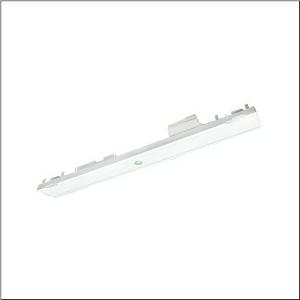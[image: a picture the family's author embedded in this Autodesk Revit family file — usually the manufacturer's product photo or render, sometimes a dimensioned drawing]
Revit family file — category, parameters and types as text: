
# Revit family: licross_r_56tl1e7c4x31_1f0a
name_source: partatom
category: Lighting Fixtures
units: mm (PartAtom-declared; Revit-internal decimal feet)

## family parameters
Cut with Voids When Loaded = No
Host = Face
Light Source = No
Part Type = Normal
Room Calculation Point = No
Round Connector Dimension = Use Diameter
Shared = No

## types (1)
- Licross® (1 x LED, 320 lm, 3.9 W, 4000K)
    Apparent Load = 4 VA
    CIE Flux Codes = 63 91 97 100 100
    Color Rendering = 70
    Color Temperature = 4000K
    Default Elevation = 1800 mm
    Description = Licross®, luminaire insert, of sheet steel, coil coated, white, length: 500mm, width: 59mm, height: 60mm, mounting height: 7..17m, emergency light element,LED rated luminous flux: 320lm, light colour: 740, control gear: CEAG, with plug, 6-pole, with phase selection, mains connection: 220..240V, AC/DC, 0/50..60Hz, rated input power: 3.9W, internal wiring halogen-free, for trunking rail, 9..14-core, for emergency light function, supply monitoring module CEAG, with address switch, choice between two emergency light lines via tool-free moving of contact pin prior to installation in trunking rail, primary light control with lens, of PMMA, primary optical cover: cover, of PMMA, light emission: direct distribution, primary light characteristic: asymmetric,  for escape and rescue routes, compatible with all CEAG STAR technology systems (ZB-S, DG-S (DualGuard-S), LP-STAR, AT-S+), protection rating (complete): IP40, insulation class (complete): insulation class I (protective earthing), certification: CE, UKCA, protection symbol: D if used in an environment without relevant dust loads, impact resistance: IK06, permissible ambient temperature for indoor applications: -20..+40°C, packaging unit: 1 piece
    Height = 60 mm  [stored 0.19685 ft]
    Lamp = 1 x LED
    Lamp Light Flux = 320 lm
    Lamp Power = 3.9 W
    Lamp count = 1
    Length = 500 mm  [stored 1.64042 ft]
    Luminous efficacy = 82 lm/W
    Manufacturer = Siteco
    ModVariant = No
    Model = 56TL1E7C4X31
    Mounting Place = Ceiling
    Mounting Type = Pendant
    Number of Poles = 1
    OnlyDefault = Yes
    Power Factor = 1
    Product Name = Licross®
    Product group = luminaire insert | ceiling pendant
    ProductGroupID = 902
    Protection Class = Protection class I
    Protection Degree = IP 40
    RLX_Detail_Level = 1
    RLX_Emergency_Light_Flux = 0 lm
    RLX_Emergency_Type = 0
    RLX_Emergency_Type_DB = No
    RlxData = <blob elided: 18013 chars, md5=ae679cd0>
    Socket = socket
    Standby Power = 0 W
    System Light Flux = 320 lm
    System Power = 4 W
    Type Comments = Product without accessories
    Type Image = l_1251804.jpg
    URL = http://relux.com
    VarID = ---
    Voltage = 0 V
    Weight = 0.00 kg
    Width = 59 mm

note: [stored X ft] marks values corroborated as IEEE doubles in the binary element streams (Revit-internal decimal feet)

## geometry (parser evidence)
native form markers: Blend x4, Sweep x13
no freeform markers — native parametric forms only
